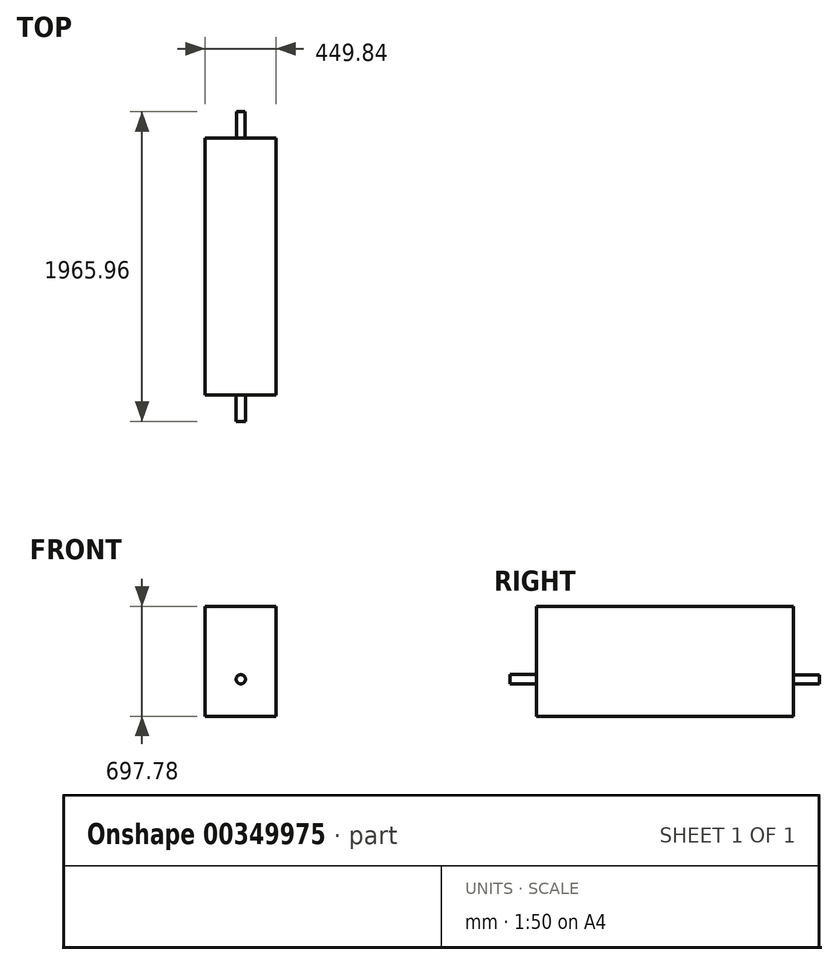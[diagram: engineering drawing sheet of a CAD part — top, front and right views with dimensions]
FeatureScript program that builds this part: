
annotation { "Feature Type Name" : "Feature", "Feature Type Description" : "" }
export const myFeature = defineFeature(function(context is Context, id is Id, definition is map)
    precondition{}
    {
        {
            var Q0;
            Q0=qCreatedBy(makeId("Front.planeOp"),FACE);
            var sketch = newSketch(context, id + "F0", { "sketchPlane" : qUnion([Q0])});
            skLineSegment(sketch, "E0.bottom", {"start": v(-226.74, 463.45) * mm, "end": v(223.1, 463.45) * mm});
            skLineSegment(sketch, "E0.top", {"start": v(-226.74, -234.33) * mm, "end": v(223.1, -234.33) * mm});
            skLineSegment(sketch, "E0.left", {"start": v(-226.74, 463.45) * mm, "end": v(-226.74, -234.33) * mm});
            skLineSegment(sketch, "E0.right", {"start": v(223.1, 463.45) * mm, "end": v(223.1, -234.33) * mm});
            skSolve(sketch);
        }
        {
            var Q0;
            Q0 = qSketchRegion(id + "F0", true);
            extrude(context, id + "F1", {"entities" : qUnion([Q0]), "depth" : 1630.68 * mm});
        }
        {
            var Q0;
            Q0=makeQuery(id+"F1.opExtrude","CAP_FACE",FACE,{"disambiguationData":[OSD([sQuery(id+"F0.wireOp",EDGE,"E0.bottom"),sQuery(id+"F0.wireOp",EDGE,"E0.top"),sQuery(id+"F0.wireOp",EDGE,"E0.left"),sQuery(id+"F0.wireOp",EDGE,"E0.right")])],"isStart":false});
            var sketch = newSketch(context, id + "F2", { "sketchPlane" : qUnion([Q0])});
            skCircle(sketch, "E1", {"center": v(0, 0) * mm, "radius": 29.58 * mm});
            skSolve(sketch);
        }
        {
            var Q0;
            Q0 = qSketchRegion(id + "F2", true);
            extrude(context, id + "F3", {"entities" : qUnion([Q0]), "operationType" : NewBodyOperationType.ADD, "depth" : 167.64 * mm});
        }
        {
            var Q0;
            Q0=makeQuery(id+"F1.opExtrude","CAP_FACE",FACE,{"disambiguationData":[OSD([sQuery(id+"F0.wireOp",EDGE,"E0.bottom"),sQuery(id+"F0.wireOp",EDGE,"E0.top"),sQuery(id+"F0.wireOp",EDGE,"E0.left"),sQuery(id+"F0.wireOp",EDGE,"E0.right")])],"isStart":true});
            var sketch = newSketch(context, id + "F4", { "sketchPlane" : qUnion([Q0])});
            skCircle(sketch, "E2", {"center": v(0, 0) * mm, "radius": 28.3 * mm});
            skSolve(sketch);
        }
        {
            var Q0;
            Q0 = qSketchRegion(id + "F4", true);
            extrude(context, id + "F5", {"entities" : qUnion([Q0]), "operationType" : NewBodyOperationType.ADD, "depth" : 167.64 * mm});
        }
    });
